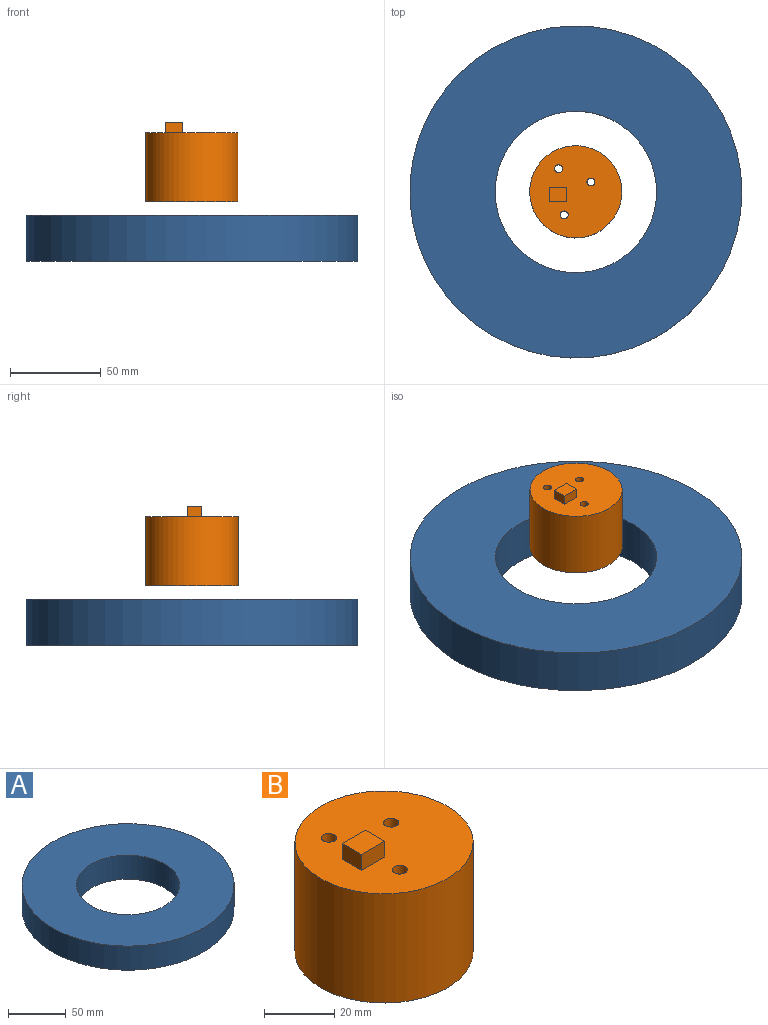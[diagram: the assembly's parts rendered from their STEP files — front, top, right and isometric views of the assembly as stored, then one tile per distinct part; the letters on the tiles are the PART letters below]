
ASSEMBLY  parts=2 mates=1
PART A: 4 faces, bbox 182.9x182.9x25.4 mm
  f0: cylinder r=44.45mm len=88.9mm, axis (0,0,-1), area 7093.9mm2, adj f2,f3
  f1: cylinder r=91.45mm len=182.89mm, axis (0,0,-1), area 14594.3mm2, adj f2,f3
  f2: plane 182.89x182.89mm, normal (0,0,1), area 20064.7mm2, adj f0,f1
  f3: plane 182.89x182.89mm, normal (0,0,-1), area 20064.7mm2, adj f0,f1
PART B: 11 faces, bbox 50.8x50.8x43.6 mm
  f0: plane 50.8x50.8mm, normal (0,0,1), area 1909.9mm2, adj f1,f3,f4,f5,f6,f7,f8,f9
  f1: cylinder r=25.4mm len=50.8mm, axis (0,0,-1), area 6080.5mm2, adj f0,f2
  f2: plane 50.8x50.8mm, normal (0,0,-1), area 1982.9mm2, adj f1,f3,f4,f5
  f3: cylinder r=2.16mm len=38.1mm, axis (0,0,1), area 516.8mm2, adj f0,f2
  f4: cylinder r=2.16mm len=38.1mm, axis (0,0,1), area 516.8mm2, adj f0,f2
  f5: cylinder r=2.16mm len=38.1mm, axis (0,0,1), area 516.8mm2, adj f0,f2
  f6: plane 9.37x5.54mm, normal (0,1,0), area 51.9mm2, adj f0,f7,f9,f10
  f7: plane 7.79x5.54mm, normal (-1,0,0), area 43.2mm2, adj f0,f6,f8,f10
  f8: plane 9.37x5.54mm, normal (0,-1,0), area 51.9mm2, adj f0,f7,f9,f10
  f9: plane 7.79x5.54mm, normal (1,0,0), area 43.2mm2, adj f0,f6,f8,f10
  f10: plane 9.37x7.79mm, normal (0,0,1), area 73mm2, adj f6,f7,f8,f9
PLACE A t=(-10.04,10.99,-12.67)mm fixed
PLACE B t=(-10.04,10.99,20.08)mm
MATE slider B.f1 <-> A.f0  axis (0,0,-1) through (-10.04,10.99,20.08)mm
